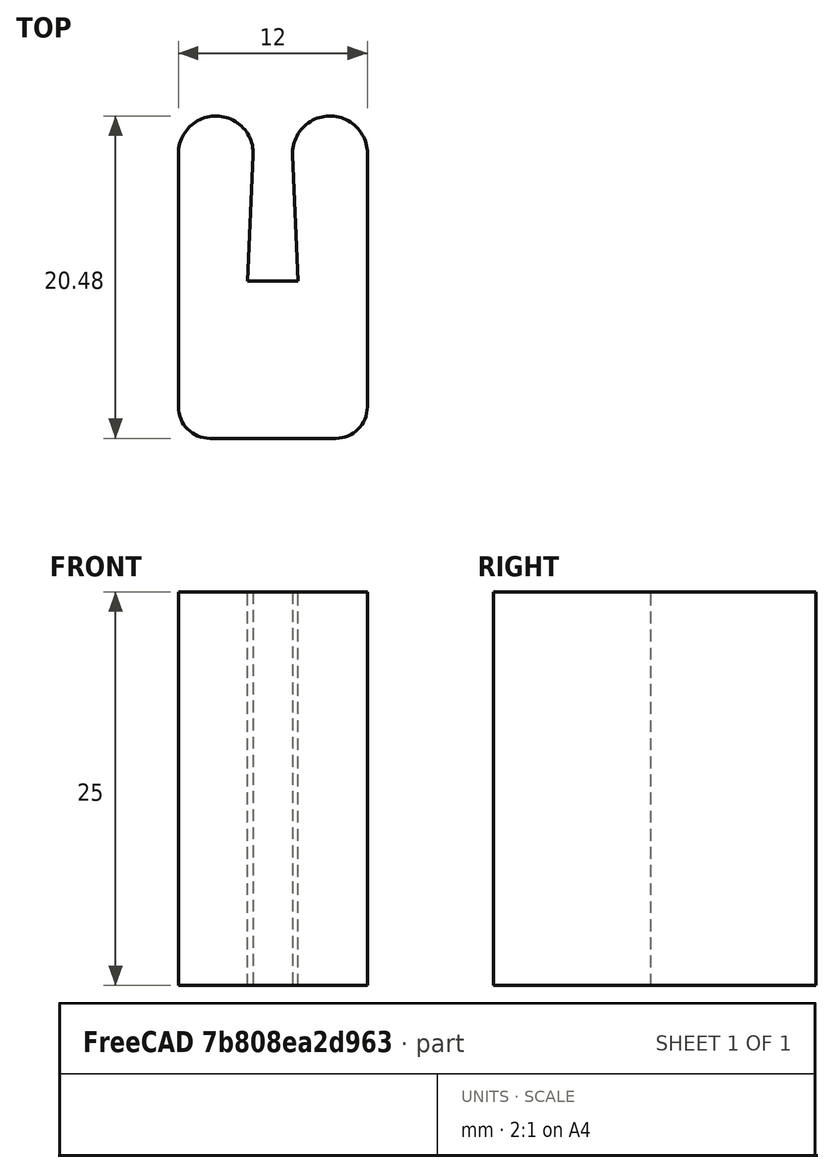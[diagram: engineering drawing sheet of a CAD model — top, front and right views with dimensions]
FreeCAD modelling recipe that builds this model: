
FCSTD DOCUMENT  (FreeCAD 1.0R39109 (Git))
Label: DoorBumper
License: All rights reserved
LicenseURL: http://en.wikipedia.org/wiki/All_rights_reserved
objects: Sketcher::SketchObject×1, PartDesign::Pad×1, PartDesign::Body×1
note: 6 computed .brp shape members not serialized (recipe doc carries the construction recipe); baked Part::Feature solids carry a one-line shape summary decoded from their .brp

FEATURE [Sketcher::SketchObject] Sketch
  ArcFitTolerance = 1e-06
  AttachmentSupport = -> [XY_Plane]
  FullyConstrained = true
  MakeInternals = false
  MapMode = 5
  sketch-geometry (14):
    g0: LineSegment StartX=-6 StartY=18.1039 StartZ=0 EndX=-6 EndY=2 EndZ=0
    g1: LineSegment StartX=-4 StartY=0 StartZ=0 EndX=4 EndY=0 EndZ=0
    g2: LineSegment StartX=6 StartY=2 StartZ=0 EndX=6 EndY=18.1039 EndZ=0
    g3: LineSegment StartX=-1.25 StartY=18 StartZ=0 EndX=-1.6 EndY=10 EndZ=0
    g4: LineSegment StartX=-1.6 StartY=10 StartZ=0 EndX=1.6 EndY=10 EndZ=0
    g5: LineSegment StartX=1.6 StartY=10 StartZ=0 EndX=1.25 EndY=18 EndZ=0
    g6: LineSegment [constr] StartX=0 StartY=0 StartZ=0 EndX=0 EndY=18 EndZ=0
    g7: ArcOfCircle CenterX=-3.62386 CenterY=18.1039 CenterZ=0 NormalX=0 NormalY=0 NormalZ=1 AngleXU=0 Radius=2.37614 StartAngle=6.23946 EndAngle=9.42478
    g8: ArcOfCircle CenterX=3.62386 CenterY=18.1039 CenterZ=0 NormalX=0 NormalY=0 NormalZ=1 AngleXU=0 Radius=2.37614 StartAngle=2e-16 EndAngle=3.18531
    g9: LineSegment [constr] StartX=-1.25 StartY=18 StartZ=0 EndX=1.25 EndY=18 EndZ=0
    g10: ArcOfCircle CenterX=-4 CenterY=2 CenterZ=0 NormalX=0 NormalY=0 NormalZ=1 AngleXU=0 Radius=2 StartAngle=3.14159 EndAngle=4.71239
    g11: GeomPoint [constr] X=-6 Y=0 Z=0
    g12: ArcOfCircle CenterX=4 CenterY=2 CenterZ=0 NormalX=0 NormalY=0 NormalZ=1 AngleXU=0 Radius=2 StartAngle=4.71239 EndAngle=6.28319
    g13: GeomPoint [constr] X=6 Y=0 Z=0
  constraints (32):
    c: Vertical(g0)
    c: Horizontal(g1)
    c: Vertical(g2)
    c: Coincident(g3,g4)
    c: Coincident(g4,g5)
    c: Symmetric(g11,g13,g6)
    c: Symmetric(g3,g4,g6)
    c: DistanceX(g4,g4) = 3.2
    c: DistanceY(g3,g3) = 8
    c: Tangent(g7,g0) = -1.5708
    c: Tangent(g2,g8) = -1.5708
    c: Tangent(g3,g7) = 1.5708
    c: Tangent(g5,g8) = 1.5708
    c: Horizontal(g4)
    c: Coincident(g9,g3)
    c: Coincident(g9,g5)
    c: Horizontal(g9)
    c: Symmetric(g3,g5,g6)
    c: DistanceX(g3,g5) = 2.5
    c: PointOnObject(g11,g0)
    c: PointOnObject(g11,g1)
    c: Tangent(g0,g10) = -1.5708
    c: Tangent(g1,g10) = -1.5708
    c: PointOnObject(g13,g1)
    c: PointOnObject(g13,g2)
    c: Tangent(g1,g12) = -1.5708
    c: Tangent(g2,g12) = -1.5708
    c: DistanceX(g11,g13) = 12
    c: DistanceY(g11,g3) = 10
    c: Equal(g10,g12)
    c: Radius(g10) = 2
    c: Coincident(g6,g-1)
FEATURE [PartDesign::Pad] Pad
  Direction = (0,0,1)
  Length = 25
  Length2 = 10
  Profile = -> Sketch
  ReferenceAxis = -> Sketch [N_Axis]
  Suppressed = false
  Type = 0
FEATURE [PartDesign::Body] Body
  AllowCompound = false
  Group = -> [Sketch,Pad]
  Origin = -> Origin
  Tip = -> Pad
